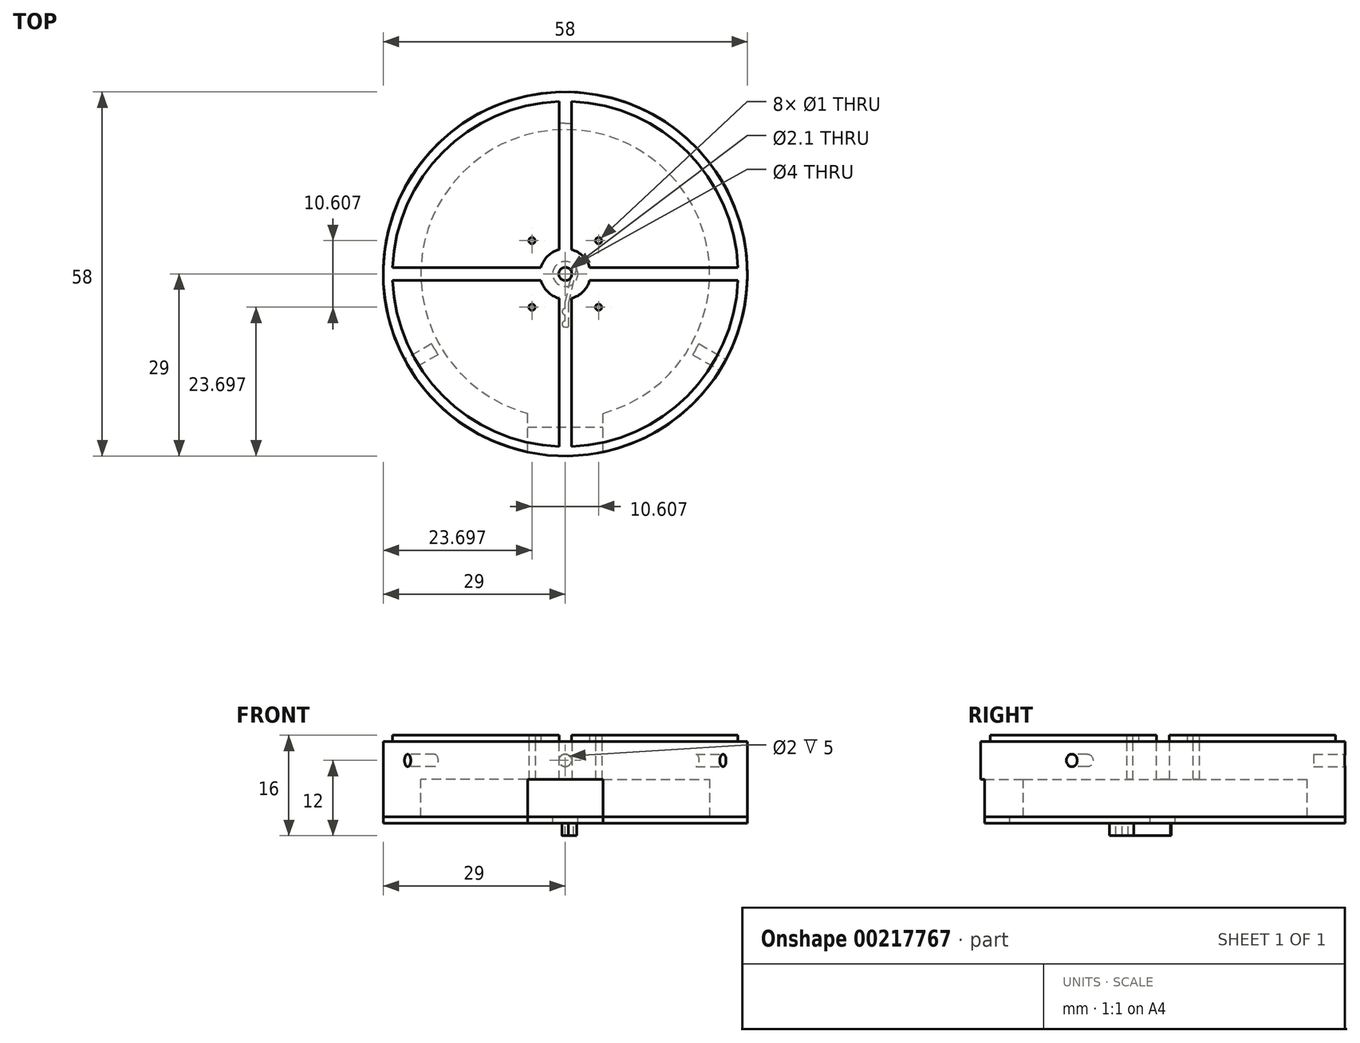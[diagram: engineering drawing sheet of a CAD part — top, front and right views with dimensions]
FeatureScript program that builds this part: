
annotation { "Feature Type Name" : "Feature", "Feature Type Description" : "" }
export const myFeature = defineFeature(function(context is Context, id is Id, definition is map)
    precondition{}
    {
        {
            var Q0;
            Q0=qCreatedBy(makeId("Top.planeOp"),FACE);
            var sketch = newSketch(context, id + "F0", { "sketchPlane" : qUnion([Q0])});
            skCircle(sketch, "E0", {"center": v(0, 0) * mm, "radius": 29 * mm});
            skCircle(sketch, "E1", {"center": v(0, 0) * mm, "radius": 7.5 * mm, "construction": true});
            skCircle(sketch, "E2", {"center": v(5.3, -5.3) * mm, "radius": 0.5 * mm});
            skLineSegment(sketch, "E3", {"start": v(5.3, -5.3) * mm, "end": v(0, -5.3) * mm, "construction": true});
            skLineSegment(sketch, "E4", {"start": v(5.3, -5.3) * mm, "end": v(5.3, 0) * mm, "construction": true});
            skCircle(sketch, "E5.1.0", {"center": v(5.3, 5.3) * mm, "radius": 0.5 * mm});
            skCircle(sketch, "E5.2.0", {"center": v(-5.3, 5.3) * mm, "radius": 0.5 * mm});
            skCircle(sketch, "E5.3.0", {"center": v(-5.3, -5.3) * mm, "radius": 0.5 * mm});
            skCircle(sketch, "E6", {"center": v(0, 0) * mm, "radius": 1.05 * mm});
            skSolve(sketch);
        }
        {
            var Q0;
            Q0=makeQuery(id+"F0.imprint","IMPRINT",FACE,{"disambiguationData":[TD([[makeQuery(id+"F0.imprint","IMPRINT",EDGE,{"derivedFrom":sQuery(id+"F0.wireOp",EDGE,"E0")}),1.0]])]});
            var Q1;
            Q1=sQuery(id+"F0.wireOp",EDGE,"E0");
            extrude(context, id + "F1", {"entities" : qUnion([Q0]), "surfaceEntities" : qUnion([Q1]), "depth" : 6 * mm});
        }
        {
            var Q0;
            Q0=makeQuery(id+"F1.opExtrude","CAP_FACE",FACE,{"disambiguationData":[OSD([sQuery(id+"F0.wireOp",EDGE,"E0")])],"isStart":false});
            var sketch = newSketch(context, id + "F2", { "sketchPlane" : qUnion([Q0])});
            skArc(sketch, "E7", {"start": v(-1, 27.48) * mm, "mid": v(-19.45, 19.45) * mm, "end": v(-27.48, 1) * mm});
            skArc(sketch, "E8", {"start": v(-1, 3.87) * mm, "mid": v(-2.83, 2.83) * mm, "end": v(-3.87, 1) * mm});
            skLineSegment(sketch, "E9", {"start": v(-27.5, 0) * mm, "end": v(27.5, 0) * mm, "construction": true});
            skLineSegment(sketch, "E10", {"start": v(0, 27.5) * mm, "end": v(0, -27.5) * mm, "construction": true});
            skLineSegment(sketch, "E11.0", {"start": v(-27.5, -1) * mm, "end": v(-3.87, -1) * mm});
            skLineSegment(sketch, "E12.0", {"start": v(-27.5, 1) * mm, "end": v(-3.87, 1) * mm});
            skLineSegment(sketch, "E13.0", {"start": v(-1, 27.5) * mm, "end": v(-1, 3.87) * mm});
            skLineSegment(sketch, "E14.0", {"start": v(1, 27.5) * mm, "end": v(1, 3.87) * mm});
            skLineSegment(sketch, "E15.trimOffspring", {"start": v(3.87, 1) * mm, "end": v(27.5, 1) * mm});
            skLineSegment(sketch, "E16.trimOffspring", {"start": v(1, -3.87) * mm, "end": v(1, -27.5) * mm});
            skLineSegment(sketch, "E17.trimOffspring", {"start": v(3.87, -1) * mm, "end": v(27.5, -1) * mm});
            skLineSegment(sketch, "E18.trimOffspring", {"start": v(-1, -3.87) * mm, "end": v(-1, -27.5) * mm});
            skArc(sketch, "E19.trimOffspring", {"start": v(-3.87, -1) * mm, "mid": v(-2.83, -2.83) * mm, "end": v(-1, -3.87) * mm});
            skArc(sketch, "E20.trimOffspring", {"start": v(1, -3.87) * mm, "mid": v(2.83, -2.83) * mm, "end": v(3.87, -1) * mm});
            skArc(sketch, "E21.trimOffspring", {"start": v(3.87, 1) * mm, "mid": v(2.83, 2.83) * mm, "end": v(1, 3.87) * mm});
            skArc(sketch, "E22.trimOffspring", {"start": v(27.48, 1) * mm, "mid": v(19.45, 19.45) * mm, "end": v(1, 27.48) * mm});
            skArc(sketch, "E23.trimOffspring", {"start": v(1, -27.48) * mm, "mid": v(19.45, -19.45) * mm, "end": v(27.48, -1) * mm});
            skArc(sketch, "E24.trimOffspring", {"start": v(-27.48, -1) * mm, "mid": v(-19.45, -19.45) * mm, "end": v(-1, -27.48) * mm});
            skCircle(sketch, "E25", {"center": v(-5.3, 5.3) * mm, "radius": 0.5 * mm});
            skCircle(sketch, "E26.1.0", {"center": v(-5.3, -5.3) * mm, "radius": 0.5 * mm});
            skCircle(sketch, "E26.2.0", {"center": v(5.3, -5.3) * mm, "radius": 0.5 * mm});
            skCircle(sketch, "E26.3.0", {"center": v(5.3, 5.3) * mm, "radius": 0.5 * mm});
            skSolve(sketch);
        }
        {
            var Q0;
            {var subQ0=sQuery(id+"F2.wireOp",EDGE,"7aQVkf6q-koz4-W3Qb-yW33-aontisj6e9hF");Q0=makeQuery(id+"F2.imprint","IMPRINT",FACE,{"disambiguationData":[TD([[makeQuery(id+"F2.imprint","IMPRINT",EDGE,{"derivedFrom":subQ0}),1.0]])]});}
            var Q1;
            Q1 = qSketchRegion(id + "F2", true);
            extrude(context, id + "F3", {"entities" : qUnion([Q0, Q1]), "depth" : 1 * mm});
        }
        {
            var Q0;
            Q0=qCreatedBy(makeId("Front.planeOp"),FACE);
            cPlane(context, id + "F4", {"entities" : qUnion([Q0]), "cplaneType" : CPlaneType.OFFSET, "offset" : 29 * mm, "oppositeDirection" : true, "width" : 150 * mm, "height" : 150 * mm});
        }
        {
            var Q0;
            Q0=qCreatedBy(id+"F4.planeOp",FACE);
            var sketch = newSketch(context, id + "F5", { "sketchPlane" : qUnion([Q0])});
            skCircle(sketch, "E27", {"center": v(0, 3) * mm, "radius": 1 * mm});
            skLineSegment(sketch, "E28", {"start": v(0, 6) * mm, "end": v(0, 0) * mm, "construction": true});
            skSolve(sketch);
        }
        {
            var Q0;
            Q0 = qSketchRegion(id + "F5", true);
            var Q1;
            Q1=sQuery(id+"F5.wireOp",EDGE,"E27");
            extrude(context, id + "F6", {"entities" : qUnion([Q0]), "surfaceEntities" : qUnion([Q1]), "depth" : 5 * mm});
        }
        {
            var Q0;
            Q0=makeQuery(id+"F6.opExtrude","SWEPT_BODY",BODY,{"disambiguationData":[OSD([sQuery(id+"F5.wireOp",EDGE,"E27")])]});
            var Q1;
            Q1=makeQuery(id+"F1.opExtrude","SWEPT_FACE",FACE,{"disambiguationData":[OSD([sQuery(id+"F0.wireOp",EDGE,"E6")])]});
            circularPattern(context, id + "F7", {"entities" : qUnion([Q0]), "axis" : qUnion([Q1]), "angle" : 360 * degree, "instanceCount" : 3, "equalSpace" : true});
        }
        {
            var Q0;
            Q0=makeQuery(id+"F7.opPattern","COPY",BODY,{"derivedFrom":makeQuery(id+"F6.opExtrude","SWEPT_BODY",BODY,{"disambiguationData":[OSD([sQuery(id+"F5.wireOp",EDGE,"E27")])]}),"instanceName":"1"});
            var Q1;
            Q1=makeQuery(id+"F6.opExtrude","SWEPT_BODY",BODY,{"disambiguationData":[OSD([sQuery(id+"F5.wireOp",EDGE,"E27")])]});
            var Q2;
            Q2=makeQuery(id+"F7.opPattern","COPY",BODY,{"derivedFrom":makeQuery(id+"F6.opExtrude","SWEPT_BODY",BODY,{"disambiguationData":[OSD([sQuery(id+"F5.wireOp",EDGE,"E27")])]}),"instanceName":"2"});
            var Q3;
            Q3=makeQuery(id+"F1.opExtrude","SWEPT_BODY",BODY,{"disambiguationData":[OSD([sQuery(id+"F0.wireOp",EDGE,"E0"),sQuery(id+"F0.wireOp",EDGE,"E2"),sQuery(id+"F0.wireOp",EDGE,"E5.1.0"),sQuery(id+"F0.wireOp",EDGE,"E5.2.0"),sQuery(id+"F0.wireOp",EDGE,"E5.3.0"),sQuery(id+"F0.wireOp",EDGE,"E6")])]});
            booleanBodies(context, id + "F8", {"operationType" : BooleanOperationType.SUBTRACTION, "tools" : qUnion([Q0, Q1, Q2]), "targets" : qUnion([Q3])});
        }
        {
            var Q0;
            Q0=makeQuery(id+"F1.opExtrude","CAP_FACE",FACE,{"disambiguationData":[OSD([sQuery(id+"F0.wireOp",EDGE,"E0"),sQuery(id+"F0.wireOp",EDGE,"E2"),sQuery(id+"F0.wireOp",EDGE,"E5.1.0"),sQuery(id+"F0.wireOp",EDGE,"E5.2.0"),sQuery(id+"F0.wireOp",EDGE,"E5.3.0"),sQuery(id+"F0.wireOp",EDGE,"E6")])],"isStart":true});
            var sketch = newSketch(context, id + "F9", { "sketchPlane" : qUnion([Q0])});
            skArc(sketch, "E29", {"start": v(-6, 28.37) * mm, "mid": v(0, -29) * mm, "end": v(6, 28.37) * mm});
            skArc(sketch, "E30", {"start": v(-6, 22.2) * mm, "mid": v(0, -23) * mm, "end": v(6, 22.2) * mm});
            skLineSegment(sketch, "E31", {"start": v(0, 29) * mm, "end": v(0, 0) * mm, "construction": true});
            skLineSegment(sketch, "E32.0", {"start": v(-6, 28.37) * mm, "end": v(-6, 22.2) * mm});
            skLineSegment(sketch, "E33.0", {"start": v(6, 28.37) * mm, "end": v(6, 22.2) * mm});
            skSolve(sketch);
        }
        {
            var Q0;
            Q0=makeQuery(id+"F9.imprint","IMPRINT",FACE,{"disambiguationData":[TD([[makeQuery(id+"F9.imprint","IMPRINT",EDGE,{"derivedFrom":sQuery(id+"F9.wireOp",EDGE,"E29")}),-1.0]])]});
            extrude(context, id + "F10", {"entities" : qUnion([Q0]), "operationType" : NewBodyOperationType.ADD, "depth" : 6 * mm});
        }
        {
            var Q0;
            Q0=makeQuery(id+"F10.opExtrude","CAP_FACE",FACE,{"disambiguationData":[OSD([sQuery(id+"F9.wireOp",EDGE,"E29"),sQuery(id+"F9.wireOp",EDGE,"E30"),sQuery(id+"F9.wireOp",EDGE,"E32.0"),sQuery(id+"F9.wireOp",EDGE,"E33.0")])],"isStart":false});
            var sketch = newSketch(context, id + "F11", { "sketchPlane" : qUnion([Q0])});
            skArc(sketch, "E34", {"start": v(-6, 28.37) * mm, "mid": v(0, -29) * mm, "end": v(6, 28.37) * mm});
            skLineSegment(sketch, "E35", {"start": v(-6, 28.37) * mm, "end": v(-6, 24.37) * mm});
            skLineSegment(sketch, "E36", {"start": v(-6, 24.37) * mm, "end": v(6, 24.37) * mm});
            skLineSegment(sketch, "E37", {"start": v(6, 24.37) * mm, "end": v(6, 28.37) * mm});
            skCircle(sketch, "E38", {"center": v(0, 0) * mm, "radius": 2 * mm});
            skSolve(sketch);
        }
        {
            var Q0;
            Q0 = qSketchRegion(id + "F11", true);
            extrude(context, id + "F12", {"entities" : qUnion([Q0]), "depth" : 1 * mm});
        }
        {
            var Q0;
            Q0=makeQuery(id+"F12.opExtrude","CAP_FACE",FACE,{"disambiguationData":[OSD([sQuery(id+"F11.wireOp",EDGE,"E34"),sQuery(id+"F11.wireOp",EDGE,"E35"),sQuery(id+"F11.wireOp",EDGE,"E36"),sQuery(id+"F11.wireOp",EDGE,"E37"),sQuery(id+"F11.wireOp",EDGE,"E38")])],"isStart":false});
            var sketch = newSketch(context, id + "F13", { "sketchPlane" : qUnion([Q0])});
            skCircle(sketch, "E39", {"center": v(0, 0) * mm, "radius": 1 * mm, "construction": true});
            skArc(sketch, "E40", {"start": v(0, 6.5) * mm, "mid": v(-0.5, 6) * mm, "end": v(0, 5.5) * mm});
            skArc(sketch, "E41", {"start": v(0, 8.5) * mm, "mid": v(-0.5, 8) * mm, "end": v(0, 7.5) * mm});
            skLineSegment(sketch, "E42", {"start": v(0, 8.5) * mm, "end": v(0, 4.5) * mm});
            skLineSegment(sketch, "E43", {"start": v(0, 4.5) * mm, "end": v(1.33, -1.35) * mm});
            skLineSegment(sketch, "E44", {"start": v(1.33, -1.35) * mm, "end": v(1.82, -1.24) * mm});
            skLineSegment(sketch, "E45", {"start": v(1.82, -1.24) * mm, "end": v(0.49, 4.61) * mm});
            skLineSegment(sketch, "E46", {"start": v(0.49, 4.61) * mm, "end": v(0.49, 8.5) * mm});
            skLineSegment(sketch, "E47", {"start": v(0.49, 8.5) * mm, "end": v(0, 8.5) * mm});
            skLineSegment(sketch, "E48", {"start": v(0, 6.5) * mm, "end": v(0, 5.5) * mm});
            skLineSegment(sketch, "E49", {"start": v(0, 8.5) * mm, "end": v(0, 7.5) * mm});
            skSolve(sketch);
        }
        {
            var Q0;
            Q0 = qSketchRegion(id + "F13", true);
            extrude(context, id + "F14", {"entities" : qUnion([Q0]), "depth" : 2 * mm});
        }
    });
